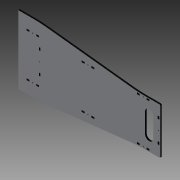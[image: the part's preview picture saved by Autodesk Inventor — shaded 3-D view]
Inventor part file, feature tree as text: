
AUTODESK INVENTOR PART (.ipt)
format: ipt  version: 2013 (Build 170138000, 138)  size: 229,888 bytes
history: native  units: in
note: dims shown in document units (in); Inventor stores cm internally (conversion verified against a paired STEP export)
features: reference x16, extrude x4, sketch x4, fillet x1
ambient origin geometry x8: Origin, YZ Plane, XZ Plane, XY Plane, X Axis, Y Axis, Z Axis, Center Point
bodies: Solid1 (feature_tree)
feature tree (25):
  extrude  "Extrusion1"  Depth=19.685in
  fillet  "Fillet1"  Radius=1.9685in
  extrude  "Extrusion2"  Depth=0.225in TaperAngle=0.0deg
  extrude  "Extrusion3"  Depth=0.1181in
  extrude  "Extrusion4"  Depth=0.1181in
  sketch  "Sketch1"  dims[d0=0.1181in d2=19.685in d3=1.9685in]
  sketch  "Sketch2"  dims[d4=1.5748in d5=0.225in d6=0.0in]
  reference  "Reference1"
  reference  "Reference2"
  reference  "Reference3"
  reference  "Reference4"
  reference  "Reference5"
  reference  "Reference6"
  reference  "Reference7"
  reference  "Reference8"
  reference  "Reference9"
  reference  "Reference10"
  reference  "Reference11"
  reference  "Reference12"
  reference  "Reference13"
  reference  "Reference14"
  sketch  "Sketch3"  dims[d7=0.1181in d8=0.1181in]
  reference  "Reference15"
  reference  "Reference16"
  sketch  "Sketch4"  dims[d10=0.1181in d11=0.1181in d12=0.1181in d13=0.1181in d14=0.1181in d15=0.1181in d16=0.225in d17=0.0in d18=0.1181in d20=0.225in d21=0.0in d22=2.7559in d25=0.5906in d26=0.9843in d27=1.0in d28=0.0in]
